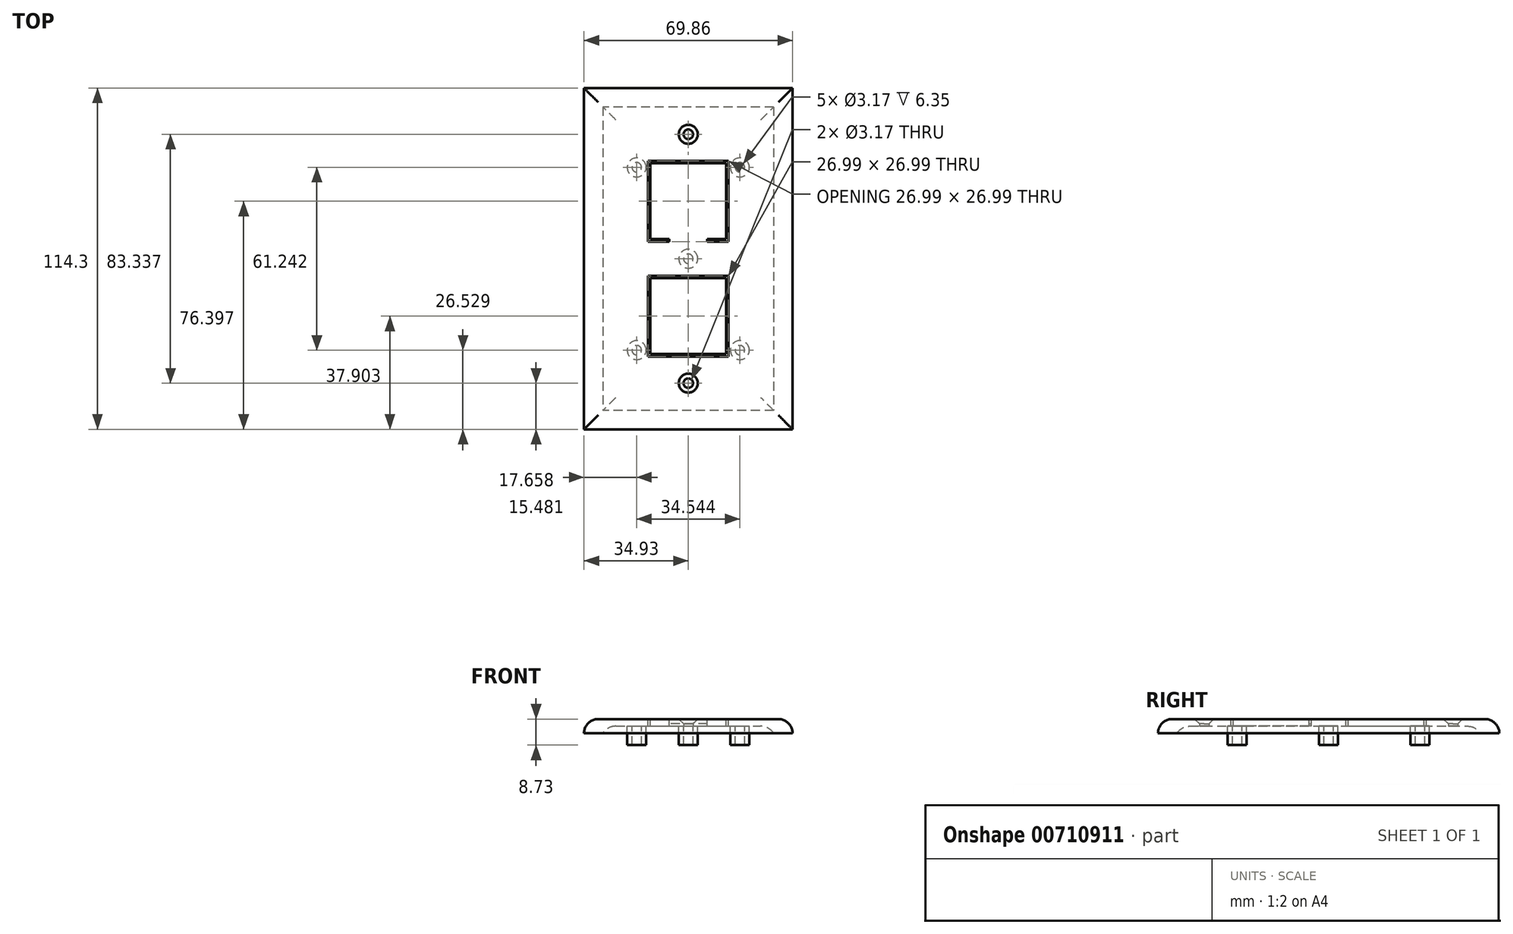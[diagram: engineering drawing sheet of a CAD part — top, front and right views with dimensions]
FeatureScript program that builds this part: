
annotation { "Feature Type Name" : "Feature", "Feature Type Description" : "" }
export const myFeature = defineFeature(function(context is Context, id is Id, definition is map)
    precondition{}
    {
        {
            var Q0;
            Q0=qCreatedBy(makeId("Top.planeOp"),FACE);
            var sketch = newSketch(context, id + "F0", { "sketchPlane" : qUnion([Q0])});
            skLineSegment(sketch, "E0.bottom", {"start": v(34.93, 57.15) * mm, "end": v(-34.93, 57.15) * mm});
            skLineSegment(sketch, "E0.top", {"start": v(34.93, -57.15) * mm, "end": v(-34.93, -57.15) * mm});
            skLineSegment(sketch, "E0.left", {"start": v(34.93, 57.15) * mm, "end": v(34.93, -57.15) * mm});
            skLineSegment(sketch, "E0.right", {"start": v(-34.93, 57.15) * mm, "end": v(-34.93, -57.15) * mm});
            skPoint(sketch, "E0.middle", {"position": v(0, 0) * mm});
            skCircle(sketch, "E1", {"center": v(0, 41.67) * mm, "radius": 1.59 * mm});
            skPoint(sketch, "E1.centerSnap0", {"position": v(0, 57.15) * mm});
            skCircle(sketch, "E2.MirrorC", {"center": v(0, -41.67) * mm, "radius": 1.59 * mm});
            skSolve(sketch);
        }
        {
            var Q0;
            Q0 = qSketchRegion(id + "F0", true);
            extrude(context, id + "F1", {"entities" : qUnion([Q0]), "depth" : 4.76 * mm, "offsetDistance" : 25.4 * mm});
        }
        {
            var Q0;
            Q0=makeQuery(id+"F1.opExtrude","CAP_EDGE",EDGE,{"disambiguationData":[OSD([sQuery(id+"F0.wireOp",EDGE,"E0.left")])],"isStart":false});
            var Q1;
            Q1=makeQuery(id+"F1.opExtrude","CAP_EDGE",EDGE,{"disambiguationData":[OSD([sQuery(id+"F0.wireOp",EDGE,"E0.top")])],"isStart":false});
            var Q2;
            Q2=makeQuery(id+"F1.opExtrude","CAP_EDGE",EDGE,{"disambiguationData":[OSD([sQuery(id+"F0.wireOp",EDGE,"E0.right")])],"isStart":false});
            var Q3;
            Q3=makeQuery(id+"F1.opExtrude","CAP_EDGE",EDGE,{"disambiguationData":[OSD([sQuery(id+"F0.wireOp",EDGE,"E0.bottom")])],"isStart":false});
            fillet(context, id + "F2", {"entities" : qUnion([Q0, Q1, Q2, Q3]), "radius" : 4.76 * mm, "tangentPropagation" : true, "allowEdgeOverflow" : false});
        }
        {
            var Q0;
            Q0=makeQuery(id+"F1.opExtrude","CAP_EDGE",EDGE,{"disambiguationData":[OSD([sQuery(id+"F0.wireOp",EDGE,"E1")])],"isStart":false});
            var Q1;
            Q1=makeQuery(id+"F1.opExtrude","CAP_EDGE",EDGE,{"disambiguationData":[OSD([sQuery(id+"F0.wireOp",EDGE,"E2.MirrorC")])],"isStart":false});
            chamfer(context, id + "F3", {"entities" : qUnion([Q0, Q1]), "width" : 1.59 * mm, "tangentPropagation" : true});
        }
        {
            var Q0;
            Q0=makeQuery(id+"F1.opExtrude","CAP_FACE",FACE,{"disambiguationData":[OSD([sQuery(id+"F0.wireOp",EDGE,"E0.bottom"),sQuery(id+"F0.wireOp",EDGE,"E0.top"),sQuery(id+"F0.wireOp",EDGE,"E0.left"),sQuery(id+"F0.wireOp",EDGE,"E0.right"),sQuery(id+"F0.wireOp",EDGE,"E1"),sQuery(id+"F0.wireOp",EDGE,"E2.MirrorC")])],"isStart":true});
            var sketch = newSketch(context, id + "F4", { "sketchPlane" : qUnion([Q0])});
            skLineSegment(sketch, "E3.0", {"start": v(28.58, 50.8) * mm, "end": v(-28.58, 50.8) * mm});
            skLineSegment(sketch, "E3.1", {"start": v(28.58, -50.8) * mm, "end": v(28.58, 50.8) * mm});
            skLineSegment(sketch, "E3.2", {"start": v(28.58, -50.8) * mm, "end": v(-28.58, -50.8) * mm});
            skLineSegment(sketch, "E3.3", {"start": v(-28.58, -50.8) * mm, "end": v(-28.58, 50.8) * mm});
            skSolve(sketch);
        }
        {
            var Q0;
            Q0 = qSketchRegion(id + "F4", true);
            extrude(context, id + "F5", {"entities" : qUnion([Q0]), "operationType" : NewBodyOperationType.REMOVE, "oppositeDirection" : true, "depth" : 2.38 * mm, "offsetDistance" : 25.4 * mm});
        }
        {
            var Q0;
            Q0=makeQuery(id+"F5.boolean.opBoolean","COPY",EDGE,{"derivedFrom":makeQuery(id+"F5.opExtrude","CAP_EDGE",EDGE,{"disambiguationData":[OSD([sQuery(id+"F4.wireOp",EDGE,"E3.1")])],"isStart":false})});
            var Q1;
            Q1=makeQuery(id+"F5.boolean.opBoolean","COPY",EDGE,{"derivedFrom":makeQuery(id+"F5.opExtrude","CAP_EDGE",EDGE,{"disambiguationData":[OSD([sQuery(id+"F4.wireOp",EDGE,"E3.0")])],"isStart":false})});
            var Q2;
            Q2=makeQuery(id+"F5.boolean.opBoolean","COPY",EDGE,{"derivedFrom":makeQuery(id+"F5.opExtrude","CAP_EDGE",EDGE,{"disambiguationData":[OSD([sQuery(id+"F4.wireOp",EDGE,"E3.3")])],"isStart":false})});
            var Q3;
            Q3=makeQuery(id+"F5.boolean.opBoolean","COPY",EDGE,{"derivedFrom":makeQuery(id+"F5.opExtrude","CAP_EDGE",EDGE,{"disambiguationData":[OSD([sQuery(id+"F4.wireOp",EDGE,"E3.2")])],"isStart":false})});
            fillet(context, id + "F6", {"entities" : qUnion([Q0, Q1, Q2, Q3]), "radius" : 5.08 * mm, "tangentPropagation" : true, "allowEdgeOverflow" : false});
        }
        {
            var Q0;
            Q0=makeQuery(id+"F1.opExtrude","CAP_FACE",FACE,{"disambiguationData":[OSD([sQuery(id+"F0.wireOp",EDGE,"E0.bottom"),sQuery(id+"F0.wireOp",EDGE,"E0.top"),sQuery(id+"F0.wireOp",EDGE,"E0.left"),sQuery(id+"F0.wireOp",EDGE,"E0.right"),sQuery(id+"F0.wireOp",EDGE,"E1"),sQuery(id+"F0.wireOp",EDGE,"E2.MirrorC")])],"isStart":false});
            var sketch = newSketch(context, id + "F7", { "sketchPlane" : qUnion([Q0])});
            skLineSegment(sketch, "E4.bottom", {"start": v(12.7, 31.95) * mm, "end": v(-12.7, 31.95) * mm});
            skLineSegment(sketch, "E4.top", {"start": v(12.7, 6.55) * mm, "end": v(-12.7, 6.55) * mm});
            skLineSegment(sketch, "E4.left", {"start": v(12.7, 31.95) * mm, "end": v(12.7, 6.55) * mm});
            skLineSegment(sketch, "E4.right", {"start": v(-12.7, 31.95) * mm, "end": v(-12.7, 6.55) * mm});
            skPoint(sketch, "E4.middle", {"position": v(0, 19.25) * mm});
            skLineSegment(sketch, "E5.0", {"start": v(13.5, 32.74) * mm, "end": v(-13.5, 32.74) * mm});
            skLineSegment(sketch, "E5.1", {"start": v(13.5, 32.74) * mm, "end": v(13.5, 5.75) * mm});
            skLineSegment(sketch, "E5.2", {"start": v(13.5, 5.75) * mm, "end": v(-13.5, 5.75) * mm});
            skLineSegment(sketch, "E5.3", {"start": v(-13.5, 32.74) * mm, "end": v(-13.5, 5.75) * mm});
            skLineSegment(sketch, "E6", {"start": v(0, 0) * mm, "end": v(0, 38.5) * mm, "construction": true});
            skPoint(sketch, "E7", {"position": v(0, 6.55) * mm});
            skLineSegment(sketch, "E8.bottom", {"start": v(-6.35, 6.55) * mm, "end": v(6.35, 6.55) * mm});
            skLineSegment(sketch, "E8.top", {"start": v(-6.35, 5.75) * mm, "end": v(6.35, 5.75) * mm});
            skLineSegment(sketch, "E8.left", {"start": v(-6.35, 6.55) * mm, "end": v(-6.35, 5.75) * mm});
            skLineSegment(sketch, "E8.right", {"start": v(6.35, 6.55) * mm, "end": v(6.35, 5.75) * mm});
            skLineSegment(sketch, "E9.MirrorCS", {"start": v(6.35, -6.55) * mm, "end": v(6.35, -5.75) * mm});
            skLineSegment(sketch, "E10.MirrorCS", {"start": v(-6.35, -6.55) * mm, "end": v(-6.35, -5.75) * mm});
            skPoint(sketch, "E11.MirrorP", {"position": v(0, -19.25) * mm});
            skLineSegment(sketch, "E12.MirrorCS", {"start": v(12.7, -31.95) * mm, "end": v(-12.7, -31.95) * mm});
            skLineSegment(sketch, "E13.MirrorCS", {"start": v(13.5, -5.75) * mm, "end": v(-13.5, -5.75) * mm});
            skLineSegment(sketch, "E14.MirrorCS", {"start": v(13.5, -32.74) * mm, "end": v(-13.5, -32.74) * mm});
            skLineSegment(sketch, "E15.MirrorCS", {"start": v(-13.5, -32.74) * mm, "end": v(-13.5, -5.75) * mm});
            skLineSegment(sketch, "E16.MirrorCS", {"start": v(-6.35, -6.55) * mm, "end": v(6.35, -6.55) * mm});
            skPoint(sketch, "E17.MirrorP", {"position": v(0, -6.55) * mm});
            skLineSegment(sketch, "E18.MirrorCS", {"start": v(12.7, -6.55) * mm, "end": v(-12.7, -6.55) * mm});
            skLineSegment(sketch, "E19.MirrorCS", {"start": v(-12.7, -31.95) * mm, "end": v(-12.7, -6.55) * mm});
            skLineSegment(sketch, "E20.MirrorCS", {"start": v(13.5, -32.74) * mm, "end": v(13.5, -5.75) * mm});
            skLineSegment(sketch, "E21.MirrorCS", {"start": v(12.7, -31.95) * mm, "end": v(12.7, -6.55) * mm});
            skLineSegment(sketch, "E22.MirrorCS", {"start": v(-6.35, -5.75) * mm, "end": v(6.35, -5.75) * mm});
            skSolve(sketch);
        }
        {
            var Q0;
            Q0=makeQuery(id+"F7.imprint","IMPRINT",FACE,{"disambiguationData":[TD([[makeQuery(id+"F7.imprint","IMPRINT",EDGE,{"derivedFrom":sQuery(id+"F7.wireOp",EDGE,"E4.bottom")}),-1.0]])]});
            var Q1;
            {var subQ3=sQuery(id+"F7.wireOp",EDGE,"E9.MirrorCS");Q1=makeQuery(id+"F7.imprint","IMPRINT",FACE,{"disambiguationData":[TD([[makeQuery(id+"F7.imprint","IMPRINT",EDGE,{"derivedFrom":subQ3}),-1.0]])]});}
            extrude(context, id + "F8", {"entities" : qUnion([Q0, Q1]), "operationType" : NewBodyOperationType.REMOVE, "endBound" : BoundingType.THROUGH_ALL, "oppositeDirection" : true, "depth" : 25.4 * mm, "offsetDistance" : 25.4 * mm});
        }
        {
            var Q0;
            Q0=makeQuery(id+"F7.imprint","IMPRINT",FACE,{"disambiguationData":[TD([[makeQuery(id+"F7.imprint","IMPRINT",EDGE,{"derivedFrom":sQuery(id+"F7.wireOp",EDGE,"E8.bottom")}),-1.0]])]});
            var Q1;
            {var subQ0=sQuery(id+"F7.wireOp",EDGE,"E9.MirrorCS");Q1=makeQuery(id+"F7.imprint","IMPRINT",FACE,{"disambiguationData":[TD([[makeQuery(id+"F7.imprint","IMPRINT",EDGE,{"derivedFrom":subQ0}),1.0]])]});}
            extrude(context, id + "F9", {"entities" : qUnion([Q0, Q1]), "operationType" : NewBodyOperationType.REMOVE, "oppositeDirection" : true, "depth" : 1.59 * mm, "offsetDistance" : 25.4 * mm});
        }
        {
            var Q0;
            Q0=makeQuery(id+"F5.boolean.opBoolean","COPY",FACE,{"derivedFrom":makeQuery(id+"F5.opExtrude","CAP_FACE",FACE,{"disambiguationData":[OSD([sQuery(id+"F4.wireOp",EDGE,"E3.0"),sQuery(id+"F4.wireOp",EDGE,"E3.1"),sQuery(id+"F4.wireOp",EDGE,"E3.2"),sQuery(id+"F4.wireOp",EDGE,"E3.3")])],"isStart":false})});
            var sketch = newSketch(context, id + "F10", { "sketchPlane" : qUnion([Q0])});
            skCircle(sketch, "E23", {"center": v(-17.27, 30.62) * mm, "radius": 3.18 * mm});
            skCircle(sketch, "E24.0.1.0", {"center": v(-17.27, -30.56) * mm, "radius": 3.18 * mm});
            skCircle(sketch, "E24.1.0.0", {"center": v(17.27, 30.62) * mm, "radius": 3.18 * mm});
            skCircle(sketch, "E24.1.1.0", {"center": v(17.27, -30.56) * mm, "radius": 3.18 * mm});
            skLineSegment(sketch, "E24.direction1", {"start": v(-17.27, 30.62) * mm, "end": v(17.27, 30.62) * mm, "construction": true});
            skLineSegment(sketch, "E24.direction2", {"start": v(-17.27, 30.62) * mm, "end": v(-17.27, -30.56) * mm, "construction": true});
            skLineSegment(sketch, "E25", {"start": v(-17.27, 30.62) * mm, "end": v(0, 0) * mm, "construction": true});
            skLineSegment(sketch, "E26", {"start": v(0, 0) * mm, "end": v(17.27, 30.62) * mm, "construction": true});
            skLineSegment(sketch, "E27", {"start": v(-17.27, -30.56) * mm, "end": v(0, 0) * mm, "construction": true});
            skLineSegment(sketch, "E28", {"start": v(-17.09, 40.08) * mm, "end": v(18.44, 40.08) * mm, "construction": true});
            skLineSegment(sketch, "E29", {"start": v(-18.56, -40.08) * mm, "end": v(18.4, -40.08) * mm, "construction": true});
            skCircle(sketch, "E30", {"center": v(-17.27, 30.62) * mm, "radius": 1.59 * mm});
            skCircle(sketch, "E31.MirrorC", {"center": v(17.27, 30.62) * mm, "radius": 1.59 * mm});
            skCircle(sketch, "E32.MirrorC", {"center": v(-17.27, -30.62) * mm, "radius": 1.59 * mm});
            skCircle(sketch, "E33.MirrorC", {"center": v(17.27, -30.62) * mm, "radius": 1.59 * mm});
            skCircle(sketch, "E34", {"center": v(0, 0) * mm, "radius": 1.59 * mm});
            skCircle(sketch, "E35", {"center": v(0, 0) * mm, "radius": 3.18 * mm});
            skSolve(sketch);
        }
        {
            var Q0;
            Q0 = qSketchRegion(id + "F10", true);
            extrude(context, id + "F11", {"entities" : qUnion([Q0]), "operationType" : NewBodyOperationType.ADD, "depth" : 6.35 * mm, "offsetDistance" : 25.4 * mm});
        }
    });
